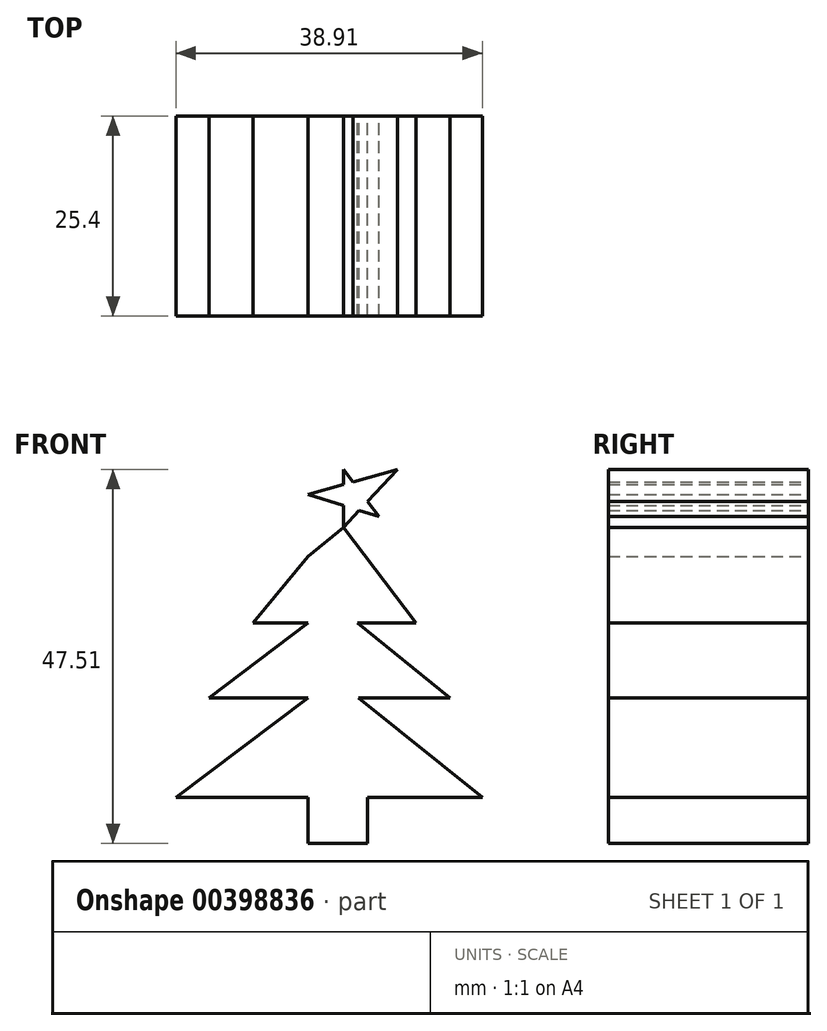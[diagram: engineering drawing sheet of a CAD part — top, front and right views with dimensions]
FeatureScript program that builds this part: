
annotation { "Feature Type Name" : "Feature", "Feature Type Description" : "" }
export const myFeature = defineFeature(function(context is Context, id is Id, definition is map)
    precondition{}
    {
        {
            var Q0;
            Q0=qCreatedBy(makeId("Front.planeOp"),FACE);
            var sketch = newSketch(context, id + "F0", { "sketchPlane" : qUnion([Q0])});
            skLineSegment(sketch, "E0", {"start": v(0, 17.93) * mm, "end": v(-7, 9.47) * mm});
            skLineSegment(sketch, "E1", {"start": v(-7, 9.47) * mm, "end": v(0, 9.47) * mm});
            skLineSegment(sketch, "E2", {"start": v(0, 9.47) * mm, "end": v(-12.53, 0) * mm});
            skLineSegment(sketch, "E3", {"start": v(-12.53, 0) * mm, "end": v(0, 0) * mm});
            skLineSegment(sketch, "E4", {"start": v(0, 0) * mm, "end": v(-16.76, -12.67) * mm});
            skLineSegment(sketch, "E5", {"start": v(-16.76, -12.67) * mm, "end": v(22.15, -12.67) * mm});
            skLineSegment(sketch, "E6", {"start": v(22.15, -12.67) * mm, "end": v(6.41, 0) * mm});
            skLineSegment(sketch, "E7", {"start": v(6.41, 0) * mm, "end": v(18.07, 0) * mm});
            skLineSegment(sketch, "E8", {"start": v(18.07, 0) * mm, "end": v(6.3, 9.47) * mm});
            skLineSegment(sketch, "E9", {"start": v(6.3, 9.47) * mm, "end": v(13.7, 9.47) * mm});
            skLineSegment(sketch, "E10", {"start": v(13.7, 9.47) * mm, "end": v(4.5, 21.66) * mm});
            skLineSegment(sketch, "E11", {"start": v(4.5, 21.66) * mm, "end": v(0, 17.93) * mm});
            skLineSegment(sketch, "E12", {"start": v(0, -12.67) * mm, "end": v(0, -18.5) * mm});
            skLineSegment(sketch, "E13", {"start": v(0, -18.5) * mm, "end": v(7.58, -18.5) * mm});
            skLineSegment(sketch, "E14", {"start": v(7.58, -18.5) * mm, "end": v(7.58, -12.67) * mm});
            skLineSegment(sketch, "E15", {"start": v(4.5, 21.66) * mm, "end": v(4.5, 29) * mm});
            skLineSegment(sketch, "E16", {"start": v(4.5, 29) * mm, "end": v(9.01, 23.02) * mm});
            skLineSegment(sketch, "E17", {"start": v(9.01, 23.02) * mm, "end": v(0, 25.8) * mm});
            skLineSegment(sketch, "E18", {"start": v(0, 25.8) * mm, "end": v(11.37, 29) * mm});
            skLineSegment(sketch, "E19", {"start": v(11.37, 29) * mm, "end": v(4.5, 21.66) * mm});
            skSolve(sketch);
        }
        {
            var Q0;
            {var subQ0=sQuery(id+"F0.wireOp",EDGE,"E12");Q0=makeQuery(id+"F0.imprint","IMPRINT",FACE,{"disambiguationData":[TD([[makeQuery(id+"F0.imprint","IMPRINT",EDGE,{"derivedFrom":subQ0}),1.0]])]});}
            var Q1;
            Q1=makeQuery(id+"F0.imprint","IMPRINT",FACE,{"disambiguationData":[TD([[makeQuery(id+"F0.imprint","IMPRINT",EDGE,{"derivedFrom":sQuery(id+"F0.wireOp",EDGE,"E0")}),1.0]])]});
            var Q2;
            {var subQ0=sQuery(id+"F0.wireOp",EDGE,"E18");var subQ1=sQuery(id+"F0.wireOp",EDGE,"E16");var subQ2=makeQuery(id+"F0.imprint","INTERSECT",VERTEX,{"derivedFrom":[subQ1,subQ0]});Q2=makeQuery(id+"F0.imprint","IMPRINT",FACE,{"disambiguationData":[TD([[makeQuery(id+"F0.imprint","IMPRINT",EDGE,{"disambiguationData":[TD([[subQ2,-1.0]])],"derivedFrom":subQ1}),1.0]])]});}
            var Q3;
            {var subQ0=sQuery(id+"F0.wireOp",EDGE,"E17");var subQ1=sQuery(id+"F0.wireOp",EDGE,"E16");var subQ2=makeQuery(id+"F0.imprint","INTERSECT",VERTEX,{"derivedFrom":[subQ1,subQ0]});Q3=makeQuery(id+"F0.imprint","IMPRINT",FACE,{"disambiguationData":[TD([[makeQuery(id+"F0.imprint","IMPRINT",EDGE,{"disambiguationData":[TD([[subQ2,1.0]])],"derivedFrom":subQ1}),-1.0]])]});}
            var Q4;
            {var subQ1=sQuery(id+"F0.wireOp",EDGE,"E15");var subQ5=sQuery(id+"F0.wireOp",EDGE,"E17");var subQ6=makeQuery(id+"F0.imprint","INTERSECT",VERTEX,{"derivedFrom":[subQ1,subQ5]});Q4=makeQuery(id+"F0.imprint","IMPRINT",FACE,{"disambiguationData":[TD([[makeQuery(id+"F0.imprint","IMPRINT",EDGE,{"disambiguationData":[TD([[subQ6,-1.0]])],"derivedFrom":subQ1}),-1.0]])]});}
            var Q5;
            {var subQ1=sQuery(id+"F0.wireOp",EDGE,"E15");var subQ3=sQuery(id+"F0.wireOp",EDGE,"E17");var subQ4=makeQuery(id+"F0.imprint","INTERSECT",VERTEX,{"derivedFrom":[subQ1,subQ3]});Q5=makeQuery(id+"F0.imprint","IMPRINT",FACE,{"disambiguationData":[TD([[makeQuery(id+"F0.imprint","IMPRINT",EDGE,{"disambiguationData":[TD([[subQ4,1.0]])],"derivedFrom":subQ3}),1.0]])]});}
            var Q6;
            {var subQ0=sQuery(id+"F0.wireOp",EDGE,"E17");var subQ1=sQuery(id+"F0.wireOp",EDGE,"E15");var subQ2=makeQuery(id+"F0.imprint","INTERSECT",VERTEX,{"derivedFrom":[subQ1,subQ0]});Q6=makeQuery(id+"F0.imprint","IMPRINT",FACE,{"disambiguationData":[TD([[makeQuery(id+"F0.imprint","IMPRINT",EDGE,{"disambiguationData":[TD([[subQ2,-1.0]])],"derivedFrom":subQ1}),1.0]])]});}
            var Q7;
            {var subQ0=sQuery(id+"F0.wireOp",EDGE,"E16");var subQ1=sQuery(id+"F0.wireOp",EDGE,"E15");var subQ2=makeQuery(id+"F0.imprint","INTERSECT",VERTEX,{"derivedFrom":[subQ1,subQ0]});Q7=makeQuery(id+"F0.imprint","IMPRINT",FACE,{"disambiguationData":[TD([[makeQuery(id+"F0.imprint","IMPRINT",EDGE,{"disambiguationData":[TD([[subQ2,1.0]])],"derivedFrom":subQ1}),-1.0]])]});}
            extrude(context, id + "F1", {"entities" : qUnion([Q0, Q1, Q2, Q3, Q4, Q5, Q6, Q7]), "depth" : 25.4 * mm});
        }
    });
